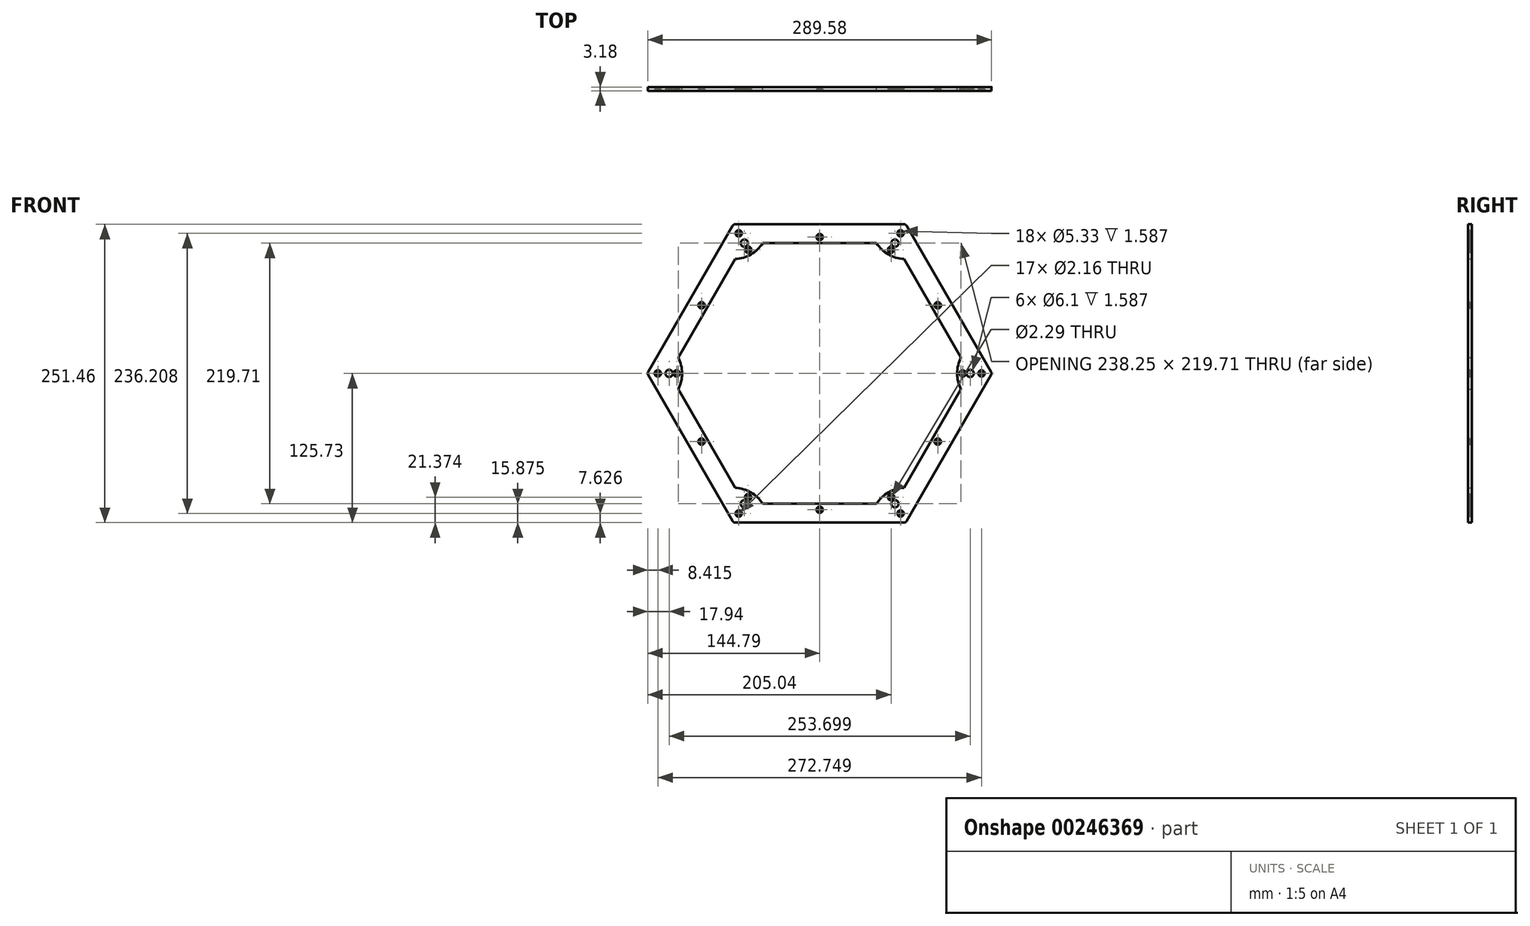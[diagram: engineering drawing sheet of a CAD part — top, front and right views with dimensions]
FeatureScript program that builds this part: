
annotation { "Feature Type Name" : "Feature", "Feature Type Description" : "" }
export const myFeature = defineFeature(function(context is Context, id is Id, definition is map)
    precondition{}
    {
        {
            var Q0;
            Q0=qCreatedBy(makeId("Front.planeOp"),FACE);
            var sketch = newSketch(context, id + "F0", { "sketchPlane" : qUnion([Q0])});
            skCircle(sketch, "E0.cCircle", {"center": v(0, 0) * mm, "radius": 125.73 * mm, "construction": true});
            skLineSegment(sketch, "E0.0", {"start": v(-72.6, 125.73) * mm, "end": v(72.6, 125.73) * mm});
            skLineSegment(sketch, "E0.1", {"start": v(72.6, 125.73) * mm, "end": v(145.18, 0) * mm});
            skLineSegment(sketch, "E0.2", {"start": v(145.18, 0) * mm, "end": v(72.6, -125.73) * mm});
            skLineSegment(sketch, "E0.3", {"start": v(72.6, -125.73) * mm, "end": v(-72.6, -125.73) * mm});
            skLineSegment(sketch, "E0.4", {"start": v(-72.6, -125.73) * mm, "end": v(-145.18, 0) * mm});
            skLineSegment(sketch, "E0.5", {"start": v(-145.18, 0) * mm, "end": v(-72.6, 125.73) * mm});
            skPoint(sketch, "E0.0.midPoint", {"position": v(0, 125.73) * mm});
            skLineSegment(sketch, "E1", {"start": v(0, 0) * mm, "end": v(-103.66, 179.55) * mm, "construction": true});
            skLineSegment(sketch, "E2", {"start": v(0, 0) * mm, "end": v(108.03, 187.1) * mm, "construction": true});
            skLineSegment(sketch, "E3", {"start": v(0, 0) * mm, "end": v(215.11, 0) * mm, "construction": true});
            skLineSegment(sketch, "E4", {"start": v(0, 0) * mm, "end": v(129.36, -224.05) * mm, "construction": true});
            skLineSegment(sketch, "E5", {"start": v(0, 0) * mm, "end": v(-137.05, -237.38) * mm, "construction": true});
            skLineSegment(sketch, "E6", {"start": v(0, 0) * mm, "end": v(-290.92, 0) * mm, "construction": true});
            skCircle(sketch, "E7.cCircle", {"center": v(0, 0) * mm, "radius": 109.86 * mm, "construction": true});
            skLineSegment(sketch, "E7.0", {"start": v(-63.42, 109.86) * mm, "end": v(63.42, 109.86) * mm});
            skLineSegment(sketch, "E7.1", {"start": v(63.42, 109.85) * mm, "end": v(126.85, 0) * mm});
            skLineSegment(sketch, "E7.2", {"start": v(126.85, 0) * mm, "end": v(63.42, -109.86) * mm});
            skLineSegment(sketch, "E7.3", {"start": v(63.42, -109.85) * mm, "end": v(-63.42, -109.86) * mm});
            skLineSegment(sketch, "E7.4", {"start": v(-63.42, -109.86) * mm, "end": v(-126.85, 0) * mm});
            skLineSegment(sketch, "E7.5", {"start": v(-126.85, 0) * mm, "end": v(-63.42, 109.86) * mm});
            skPoint(sketch, "E7.0.midPoint", {"position": v(0, 109.86) * mm});
            skCircle(sketch, "E8", {"center": v(-72.6, 125.73) * mm, "radius": 29.3 * mm});
            skCircle(sketch, "E9", {"center": v(72.6, 125.73) * mm, "radius": 29.3 * mm});
            skCircle(sketch, "E10", {"center": v(145.18, 0) * mm, "radius": 29.3 * mm});
            skCircle(sketch, "E11", {"center": v(72.6, -125.73) * mm, "radius": 29.3 * mm});
            skCircle(sketch, "E12", {"center": v(-72.6, -125.73) * mm, "radius": 29.3 * mm});
            skCircle(sketch, "E13", {"center": v(-145.18, 0) * mm, "radius": 29.3 * mm});
            skCircle(sketch, "E14", {"center": v(0, 0) * mm, "radius": 115.89 * mm, "construction": true});
            skSolve(sketch);
        }
        {
            var Q0;
            {var subQ0=sQuery(id+"F0.wireOp",EDGE,"E8");var subQ1=sQuery(id+"F0.wireOp",EDGE,"E0.0");var subQ2=makeQuery(id+"F0.imprint","INTERSECT",VERTEX,{"derivedFrom":[subQ1,subQ0]});Q0=makeQuery(id+"F0.imprint","IMPRINT",FACE,{"disambiguationData":[TD([[makeQuery(id+"F0.imprint","IMPRINT",EDGE,{"disambiguationData":[TD([[subQ2,-1.0]])],"derivedFrom":subQ1}),-1.0]])]});}
            var Q1;
            {var subQ6=sQuery(id+"F0.wireOp",EDGE,"E0.0");var subQ8=sQuery(id+"F0.wireOp",EDGE,"E0.5");var subQ9=makeQuery(id+"F0.imprint","INTERSECT",VERTEX,{"derivedFrom":[subQ6,subQ8]});Q1=makeQuery(id+"F0.imprint","IMPRINT",FACE,{"disambiguationData":[TD([[makeQuery(id+"F0.imprint","IMPRINT",EDGE,{"disambiguationData":[TD([[subQ9,-1.0]])],"derivedFrom":subQ6}),-1.0]])]});}
            var Q2;
            {var subQ0=sQuery(id+"F0.wireOp",EDGE,"E13");var subQ1=sQuery(id+"F0.wireOp",EDGE,"E0.5");var subQ2=makeQuery(id+"F0.imprint","INTERSECT",VERTEX,{"derivedFrom":[subQ1,subQ0]});Q2=makeQuery(id+"F0.imprint","IMPRINT",FACE,{"disambiguationData":[TD([[makeQuery(id+"F0.imprint","IMPRINT",EDGE,{"disambiguationData":[TD([[subQ2,-1.0]])],"derivedFrom":subQ1}),-1.0]])]});}
            var Q3;
            {var subQ6=sQuery(id+"F0.wireOp",EDGE,"E0.5");var subQ7=sQuery(id+"F0.wireOp",EDGE,"E0.4");var subQ8=makeQuery(id+"F0.imprint","INTERSECT",VERTEX,{"derivedFrom":[subQ7,subQ6]});Q3=makeQuery(id+"F0.imprint","IMPRINT",FACE,{"disambiguationData":[TD([[makeQuery(id+"F0.imprint","IMPRINT",EDGE,{"disambiguationData":[TD([[subQ8,1.0]])],"derivedFrom":subQ7}),-1.0]])]});}
            var Q4;
            {var subQ0=sQuery(id+"F0.wireOp",EDGE,"E7.5");var subQ1=sQuery(id+"F0.wireOp",EDGE,"E7.4");var subQ2=makeQuery(id+"F0.imprint","INTERSECT",VERTEX,{"derivedFrom":[subQ1,subQ0]});Q4=makeQuery(id+"F0.imprint","IMPRINT",FACE,{"disambiguationData":[TD([[makeQuery(id+"F0.imprint","IMPRINT",EDGE,{"disambiguationData":[TD([[subQ2,1.0]])],"derivedFrom":subQ1}),-1.0]])]});}
            var Q5;
            {var subQ0=sQuery(id+"F0.wireOp",EDGE,"E7.5");var subQ1=sQuery(id+"F0.wireOp",EDGE,"E7.0");var subQ2=makeQuery(id+"F0.imprint","INTERSECT",VERTEX,{"derivedFrom":[subQ1,subQ0]});Q5=makeQuery(id+"F0.imprint","IMPRINT",FACE,{"disambiguationData":[TD([[makeQuery(id+"F0.imprint","IMPRINT",EDGE,{"disambiguationData":[TD([[subQ2,-1.0]])],"derivedFrom":subQ1}),-1.0]])]});}
            var Q6;
            {var subQ0=sQuery(id+"F0.wireOp",EDGE,"E7.1");var subQ1=sQuery(id+"F0.wireOp",EDGE,"E7.0");var subQ2=makeQuery(id+"F0.imprint","INTERSECT",VERTEX,{"derivedFrom":[subQ1,subQ0]});Q6=makeQuery(id+"F0.imprint","IMPRINT",FACE,{"disambiguationData":[TD([[makeQuery(id+"F0.imprint","IMPRINT",EDGE,{"disambiguationData":[TD([[subQ2,1.0]])],"derivedFrom":subQ1}),-1.0]])]});}
            var Q7;
            {var subQ6=sQuery(id+"F0.wireOp",EDGE,"E0.1");var subQ7=sQuery(id+"F0.wireOp",EDGE,"E0.0");var subQ8=makeQuery(id+"F0.imprint","INTERSECT",VERTEX,{"derivedFrom":[subQ7,subQ6]});Q7=makeQuery(id+"F0.imprint","IMPRINT",FACE,{"disambiguationData":[TD([[makeQuery(id+"F0.imprint","IMPRINT",EDGE,{"disambiguationData":[TD([[subQ8,1.0]])],"derivedFrom":subQ7}),-1.0]])]});}
            var Q8;
            {var subQ0=sQuery(id+"F0.wireOp",EDGE,"E9");var subQ1=sQuery(id+"F0.wireOp",EDGE,"E0.1");var subQ2=makeQuery(id+"F0.imprint","INTERSECT",VERTEX,{"derivedFrom":[subQ1,subQ0]});Q8=makeQuery(id+"F0.imprint","IMPRINT",FACE,{"disambiguationData":[TD([[makeQuery(id+"F0.imprint","IMPRINT",EDGE,{"disambiguationData":[TD([[subQ2,-1.0]])],"derivedFrom":subQ1}),-1.0]])]});}
            var Q9;
            {var subQ0=sQuery(id+"F0.wireOp",EDGE,"E7.2");var subQ1=sQuery(id+"F0.wireOp",EDGE,"E7.1");var subQ2=makeQuery(id+"F0.imprint","INTERSECT",VERTEX,{"derivedFrom":[subQ1,subQ0]});Q9=makeQuery(id+"F0.imprint","IMPRINT",FACE,{"disambiguationData":[TD([[makeQuery(id+"F0.imprint","IMPRINT",EDGE,{"disambiguationData":[TD([[subQ2,1.0]])],"derivedFrom":subQ1}),-1.0]])]});}
            var Q10;
            {var subQ5=sQuery(id+"F0.wireOp",EDGE,"E0.2");var subQ6=sQuery(id+"F0.wireOp",EDGE,"E0.1");var subQ7=makeQuery(id+"F0.imprint","INTERSECT",VERTEX,{"derivedFrom":[subQ6,subQ5]});Q10=makeQuery(id+"F0.imprint","IMPRINT",FACE,{"disambiguationData":[TD([[makeQuery(id+"F0.imprint","IMPRINT",EDGE,{"disambiguationData":[TD([[subQ7,1.0]])],"derivedFrom":subQ6}),-1.0]])]});}
            var Q11;
            {var subQ0=sQuery(id+"F0.wireOp",EDGE,"E10");var subQ1=sQuery(id+"F0.wireOp",EDGE,"E0.2");var subQ2=makeQuery(id+"F0.imprint","INTERSECT",VERTEX,{"derivedFrom":[subQ1,subQ0]});Q11=makeQuery(id+"F0.imprint","IMPRINT",FACE,{"disambiguationData":[TD([[makeQuery(id+"F0.imprint","IMPRINT",EDGE,{"disambiguationData":[TD([[subQ2,-1.0]])],"derivedFrom":subQ1}),-1.0]])]});}
            var Q12;
            {var subQ6=sQuery(id+"F0.wireOp",EDGE,"E0.3");var subQ7=sQuery(id+"F0.wireOp",EDGE,"E0.2");var subQ8=makeQuery(id+"F0.imprint","INTERSECT",VERTEX,{"derivedFrom":[subQ7,subQ6]});Q12=makeQuery(id+"F0.imprint","IMPRINT",FACE,{"disambiguationData":[TD([[makeQuery(id+"F0.imprint","IMPRINT",EDGE,{"disambiguationData":[TD([[subQ8,1.0]])],"derivedFrom":subQ7}),-1.0]])]});}
            var Q13;
            {var subQ0=sQuery(id+"F0.wireOp",EDGE,"E7.3");var subQ1=sQuery(id+"F0.wireOp",EDGE,"E7.2");var subQ2=makeQuery(id+"F0.imprint","INTERSECT",VERTEX,{"derivedFrom":[subQ1,subQ0]});Q13=makeQuery(id+"F0.imprint","IMPRINT",FACE,{"disambiguationData":[TD([[makeQuery(id+"F0.imprint","IMPRINT",EDGE,{"disambiguationData":[TD([[subQ2,1.0]])],"derivedFrom":subQ1}),-1.0]])]});}
            var Q14;
            {var subQ0=sQuery(id+"F0.wireOp",EDGE,"E11");var subQ1=sQuery(id+"F0.wireOp",EDGE,"E0.3");var subQ2=makeQuery(id+"F0.imprint","INTERSECT",VERTEX,{"derivedFrom":[subQ1,subQ0]});Q14=makeQuery(id+"F0.imprint","IMPRINT",FACE,{"disambiguationData":[TD([[makeQuery(id+"F0.imprint","IMPRINT",EDGE,{"disambiguationData":[TD([[subQ2,-1.0]])],"derivedFrom":subQ1}),-1.0]])]});}
            var Q15;
            {var subQ6=sQuery(id+"F0.wireOp",EDGE,"E0.4");var subQ8=sQuery(id+"F0.wireOp",EDGE,"E0.3");var subQ9=makeQuery(id+"F0.imprint","INTERSECT",VERTEX,{"derivedFrom":[subQ8,subQ6]});Q15=makeQuery(id+"F0.imprint","IMPRINT",FACE,{"disambiguationData":[TD([[makeQuery(id+"F0.imprint","IMPRINT",EDGE,{"disambiguationData":[TD([[subQ9,1.0]])],"derivedFrom":subQ8}),-1.0]])]});}
            var Q16;
            {var subQ0=sQuery(id+"F0.wireOp",EDGE,"E7.4");var subQ1=sQuery(id+"F0.wireOp",EDGE,"E7.3");var subQ2=makeQuery(id+"F0.imprint","INTERSECT",VERTEX,{"derivedFrom":[subQ1,subQ0]});Q16=makeQuery(id+"F0.imprint","IMPRINT",FACE,{"disambiguationData":[TD([[makeQuery(id+"F0.imprint","IMPRINT",EDGE,{"disambiguationData":[TD([[subQ2,1.0]])],"derivedFrom":subQ1}),-1.0]])]});}
            var Q17;
            {var subQ0=sQuery(id+"F0.wireOp",EDGE,"E12");var subQ1=sQuery(id+"F0.wireOp",EDGE,"E0.4");var subQ2=makeQuery(id+"F0.imprint","INTERSECT",VERTEX,{"derivedFrom":[subQ1,subQ0]});Q17=makeQuery(id+"F0.imprint","IMPRINT",FACE,{"disambiguationData":[TD([[makeQuery(id+"F0.imprint","IMPRINT",EDGE,{"disambiguationData":[TD([[subQ2,-1.0]])],"derivedFrom":subQ1}),-1.0]])]});}
            extrude(context, id + "F1", {"entities" : qUnion([Q0, Q1, Q2, Q3, Q4, Q5, Q6, Q7, Q8, Q9, Q10, Q11, Q12, Q13, Q14, Q15, Q16, Q17]), "depth" : 3.17 * mm});
        }
        {
            var Q0;
            Q0=makeQuery(id+"F1.opExtrude","CAP_FACE",FACE,{"disambiguationData":[OSD([sQuery(id+"F0.wireOp",EDGE,"E0.0"),sQuery(id+"F0.wireOp",EDGE,"E0.1"),sQuery(id+"F0.wireOp",EDGE,"E0.2"),sQuery(id+"F0.wireOp",EDGE,"E0.3"),sQuery(id+"F0.wireOp",EDGE,"E0.4"),sQuery(id+"F0.wireOp",EDGE,"E0.5"),sQuery(id+"F0.wireOp",EDGE,"E7.0"),sQuery(id+"F0.wireOp",EDGE,"E7.1"),sQuery(id+"F0.wireOp",EDGE,"E7.2"),sQuery(id+"F0.wireOp",EDGE,"E7.3"),sQuery(id+"F0.wireOp",EDGE,"E7.4"),sQuery(id+"F0.wireOp",EDGE,"E7.5"),sQuery(id+"F0.wireOp",EDGE,"E8"),sQuery(id+"F0.wireOp",EDGE,"E9"),sQuery(id+"F0.wireOp",EDGE,"E10"),sQuery(id+"F0.wireOp",EDGE,"E11"),sQuery(id+"F0.wireOp",EDGE,"E12"),sQuery(id+"F0.wireOp",EDGE,"E13")])],"isStart":false});
            var sketch = newSketch(context, id + "F2", { "sketchPlane" : qUnion([Q0])});
            skCircle(sketch, "E15", {"center": v(-63.42, 109.86) * mm, "radius": 3.05 * mm});
            skCircle(sketch, "E16", {"center": v(63.42, 109.86) * mm, "radius": 3.05 * mm});
            skCircle(sketch, "E17", {"center": v(-126.85, 0) * mm, "radius": 3.05 * mm});
            skCircle(sketch, "E18", {"center": v(-63.42, -109.86) * mm, "radius": 3.05 * mm});
            skCircle(sketch, "E19", {"center": v(63.42, -109.85) * mm, "radius": 3.05 * mm});
            skCircle(sketch, "E20", {"center": v(126.85, 0) * mm, "radius": 3.05 * mm});
            skSolve(sketch);
        }
        {
            var Q0;
            Q0 = qSketchRegion(id + "F2", true);
            extrude(context, id + "F3", {"entities" : qUnion([Q0]), "operationType" : NewBodyOperationType.REMOVE, "oppositeDirection" : true, "depth" : 1.59 * mm});
        }
        {
            var Q0;
            Q0=makeQuery(id+"F1.opExtrude","CAP_FACE",FACE,{"disambiguationData":[OSD([sQuery(id+"F0.wireOp",EDGE,"E0.0"),sQuery(id+"F0.wireOp",EDGE,"E0.1"),sQuery(id+"F0.wireOp",EDGE,"E0.2"),sQuery(id+"F0.wireOp",EDGE,"E0.3"),sQuery(id+"F0.wireOp",EDGE,"E0.4"),sQuery(id+"F0.wireOp",EDGE,"E0.5"),sQuery(id+"F0.wireOp",EDGE,"E7.0"),sQuery(id+"F0.wireOp",EDGE,"E7.1"),sQuery(id+"F0.wireOp",EDGE,"E7.2"),sQuery(id+"F0.wireOp",EDGE,"E7.3"),sQuery(id+"F0.wireOp",EDGE,"E7.4"),sQuery(id+"F0.wireOp",EDGE,"E7.5"),sQuery(id+"F0.wireOp",EDGE,"E8"),sQuery(id+"F0.wireOp",EDGE,"E9"),sQuery(id+"F0.wireOp",EDGE,"E10"),sQuery(id+"F0.wireOp",EDGE,"E11"),sQuery(id+"F0.wireOp",EDGE,"E12"),sQuery(id+"F0.wireOp",EDGE,"E13")])],"isStart":false});
            var sketch = newSketch(context, id + "F4", { "sketchPlane" : qUnion([Q0])});
            skCircle(sketch, "E21", {"center": v(-60.25, 104.36) * mm, "radius": 1.08 * mm});
            skLineSegment(sketch, "E22", {"start": v(-63.42, 109.86) * mm, "end": v(-60.25, 104.36) * mm, "construction": true});
            skLineSegment(sketch, "E23", {"start": v(63.42, 109.86) * mm, "end": v(60.25, 104.36) * mm, "construction": true});
            skLineSegment(sketch, "E24", {"start": v(126.85, 0) * mm, "end": v(120.5, 0) * mm, "construction": true});
            skLineSegment(sketch, "E25", {"start": v(63.42, -109.86) * mm, "end": v(60.25, -104.36) * mm, "construction": true});
            skLineSegment(sketch, "E26", {"start": v(-63.42, -109.86) * mm, "end": v(-60.25, -104.36) * mm, "construction": true});
            skLineSegment(sketch, "E27", {"start": v(-126.85, 0) * mm, "end": v(-120.5, 0) * mm, "construction": true});
            skCircle(sketch, "E28", {"center": v(60.25, 104.36) * mm, "radius": 1.08 * mm});
            skCircle(sketch, "E29", {"center": v(120.5, 0) * mm, "radius": 1.08 * mm});
            skCircle(sketch, "E30", {"center": v(60.25, -104.36) * mm, "radius": 1.14 * mm});
            skCircle(sketch, "E31", {"center": v(-60.25, -104.36) * mm, "radius": 1.08 * mm});
            skCircle(sketch, "E32", {"center": v(-120.5, 0) * mm, "radius": 1.08 * mm});
            skCircle(sketch, "E33", {"center": v(-120.5, 0) * mm, "radius": 2.67 * mm});
            skCircle(sketch, "E34", {"center": v(-60.25, 104.36) * mm, "radius": 2.67 * mm});
            skCircle(sketch, "E35", {"center": v(60.25, 104.36) * mm, "radius": 2.67 * mm});
            skCircle(sketch, "E36", {"center": v(120.5, 0) * mm, "radius": 2.67 * mm});
            skCircle(sketch, "E37", {"center": v(60.25, -104.36) * mm, "radius": 2.67 * mm});
            skCircle(sketch, "E38", {"center": v(-60.25, -104.36) * mm, "radius": 2.67 * mm});
            skCircle(sketch, "E39", {"center": v(-68.19, 118.1) * mm, "radius": 2.67 * mm});
            skLineSegment(sketch, "E40", {"start": v(-63.42, 109.86) * mm, "end": v(-68.19, 118.1) * mm, "construction": true});
            skCircle(sketch, "E41", {"center": v(-68.19, 118.1) * mm, "radius": 1.08 * mm});
            skLineSegment(sketch, "E42", {"start": v(63.42, 109.86) * mm, "end": v(68.19, 118.1) * mm, "construction": true});
            skCircle(sketch, "E43", {"center": v(68.19, 118.1) * mm, "radius": 2.67 * mm});
            skCircle(sketch, "E44", {"center": v(68.19, 118.1) * mm, "radius": 1.08 * mm});
            skLineSegment(sketch, "E45", {"start": v(-126.85, 0) * mm, "end": v(-136.37, 0) * mm, "construction": true});
            skCircle(sketch, "E46", {"center": v(-136.37, 0) * mm, "radius": 2.67 * mm});
            skCircle(sketch, "E47", {"center": v(-136.37, 0) * mm, "radius": 1.08 * mm});
            skLineSegment(sketch, "E48", {"start": v(-63.42, -109.86) * mm, "end": v(-68.19, -118.1) * mm, "construction": true});
            skCircle(sketch, "E49", {"center": v(-68.19, -118.1) * mm, "radius": 2.67 * mm});
            skCircle(sketch, "E50", {"center": v(-68.19, -118.1) * mm, "radius": 1.08 * mm});
            skLineSegment(sketch, "E51", {"start": v(126.85, 0) * mm, "end": v(136.37, 0) * mm, "construction": true});
            skCircle(sketch, "E52", {"center": v(136.37, 0) * mm, "radius": 2.67 * mm});
            skCircle(sketch, "E53", {"center": v(136.37, 0) * mm, "radius": 1.08 * mm});
            skLineSegment(sketch, "E54", {"start": v(63.42, -109.86) * mm, "end": v(68.19, -118.1) * mm, "construction": true});
            skCircle(sketch, "E55", {"center": v(68.19, -118.1) * mm, "radius": 2.67 * mm});
            skCircle(sketch, "E56", {"center": v(68.19, -118.1) * mm, "radius": 1.08 * mm});
            skCircle(sketch, "E57", {"center": v(0, 114.94) * mm, "radius": 2.67 * mm});
            skCircle(sketch, "E58", {"center": v(0, 114.94) * mm, "radius": 1.08 * mm});
            skCircle(sketch, "E59.1.0", {"center": v(-99.54, 57.47) * mm, "radius": 1.08 * mm});
            skCircle(sketch, "E59.1.1", {"center": v(-99.54, 57.47) * mm, "radius": 2.67 * mm});
            skCircle(sketch, "E59.2.0", {"center": v(-99.54, -57.47) * mm, "radius": 1.08 * mm});
            skCircle(sketch, "E59.2.1", {"center": v(-99.54, -57.47) * mm, "radius": 2.67 * mm});
            skCircle(sketch, "E59.3.0", {"center": v(0, -114.94) * mm, "radius": 1.08 * mm});
            skCircle(sketch, "E59.3.1", {"center": v(0, -114.94) * mm, "radius": 2.67 * mm});
            skCircle(sketch, "E59.4.0", {"center": v(99.54, -57.47) * mm, "radius": 1.08 * mm});
            skCircle(sketch, "E59.4.1", {"center": v(99.54, -57.47) * mm, "radius": 2.67 * mm});
            skCircle(sketch, "E59.5.0", {"center": v(99.54, 57.47) * mm, "radius": 1.08 * mm});
            skCircle(sketch, "E59.5.1", {"center": v(99.54, 57.47) * mm, "radius": 2.67 * mm});
            skPoint(sketch, "E59.center", {"position": v(0, 0) * mm});
            skLineSegment(sketch, "E60", {"start": v(0, 0) * mm, "end": v(99.54, 57.47) * mm, "construction": true});
            skLineSegment(sketch, "E61", {"start": v(0, 0) * mm, "end": v(0, -114.94) * mm, "construction": true});
            skLineSegment(sketch, "E62", {"start": v(0, 0) * mm, "end": v(99.54, -57.47) * mm, "construction": true});
            skLineSegment(sketch, "E63", {"start": v(0, 0) * mm, "end": v(-99.54, -57.47) * mm, "construction": true});
            skLineSegment(sketch, "E64", {"start": v(0, 0) * mm, "end": v(0, 114.94) * mm, "construction": true});
            skLineSegment(sketch, "E65", {"start": v(0, 0) * mm, "end": v(-99.54, 57.47) * mm, "construction": true});
            skSolve(sketch);
        }
        {
            var Q0;
            Q0=makeQuery(id+"F4.imprint","IMPRINT",FACE,{"disambiguationData":[TD([[makeQuery(id+"F4.imprint","IMPRINT",EDGE,{"derivedFrom":sQuery(id+"F4.wireOp",EDGE,"E32")}),-1.0]])]});
            var Q1;
            Q1=makeQuery(id+"F4.imprint","IMPRINT",FACE,{"disambiguationData":[TD([[makeQuery(id+"F4.imprint","IMPRINT",EDGE,{"derivedFrom":sQuery(id+"F4.wireOp",EDGE,"E21")}),-1.0]])]});
            var Q2;
            Q2=makeQuery(id+"F4.imprint","IMPRINT",FACE,{"disambiguationData":[TD([[makeQuery(id+"F4.imprint","IMPRINT",EDGE,{"derivedFrom":sQuery(id+"F4.wireOp",EDGE,"E28")}),-1.0]])]});
            var Q3;
            Q3=makeQuery(id+"F4.imprint","IMPRINT",FACE,{"disambiguationData":[TD([[makeQuery(id+"F4.imprint","IMPRINT",EDGE,{"derivedFrom":sQuery(id+"F4.wireOp",EDGE,"E29")}),-1.0]])]});
            var Q4;
            Q4=makeQuery(id+"F4.imprint","IMPRINT",FACE,{"disambiguationData":[TD([[makeQuery(id+"F4.imprint","IMPRINT",EDGE,{"derivedFrom":sQuery(id+"F4.wireOp",EDGE,"E30")}),-1.0]])]});
            var Q5;
            Q5=makeQuery(id+"F4.imprint","IMPRINT",FACE,{"disambiguationData":[TD([[makeQuery(id+"F4.imprint","IMPRINT",EDGE,{"derivedFrom":sQuery(id+"F4.wireOp",EDGE,"E31")}),-1.0]])]});
            var Q6;
            Q6=makeQuery(id+"F4.imprint","IMPRINT",FACE,{"disambiguationData":[TD([[makeQuery(id+"F4.imprint","IMPRINT",EDGE,{"derivedFrom":sQuery(id+"F4.wireOp",EDGE,"E49")}),1.0]])]});
            var Q7;
            Q7=makeQuery(id+"F4.imprint","IMPRINT",FACE,{"disambiguationData":[TD([[makeQuery(id+"F4.imprint","IMPRINT",EDGE,{"derivedFrom":sQuery(id+"F4.wireOp",EDGE,"E55")}),1.0]])]});
            var Q8;
            Q8=makeQuery(id+"F4.imprint","IMPRINT",FACE,{"disambiguationData":[TD([[makeQuery(id+"F4.imprint","IMPRINT",EDGE,{"derivedFrom":sQuery(id+"F4.wireOp",EDGE,"E52")}),1.0]])]});
            var Q9;
            Q9=makeQuery(id+"F4.imprint","IMPRINT",FACE,{"disambiguationData":[TD([[makeQuery(id+"F4.imprint","IMPRINT",EDGE,{"derivedFrom":sQuery(id+"F4.wireOp",EDGE,"E43")}),1.0]])]});
            var Q10;
            Q10=makeQuery(id+"F4.imprint","IMPRINT",FACE,{"disambiguationData":[TD([[makeQuery(id+"F4.imprint","IMPRINT",EDGE,{"derivedFrom":sQuery(id+"F4.wireOp",EDGE,"E39")}),1.0]])]});
            var Q11;
            Q11=makeQuery(id+"F4.imprint","IMPRINT",FACE,{"disambiguationData":[TD([[makeQuery(id+"F4.imprint","IMPRINT",EDGE,{"derivedFrom":sQuery(id+"F4.wireOp",EDGE,"E46")}),1.0]])]});
            var Q12;
            Q12=makeQuery(id+"F4.imprint","IMPRINT",FACE,{"disambiguationData":[TD([[makeQuery(id+"F4.imprint","IMPRINT",EDGE,{"derivedFrom":sQuery(id+"F4.wireOp",EDGE,"E59.1.0")}),-1.0]])]});
            var Q13;
            Q13=makeQuery(id+"F4.imprint","IMPRINT",FACE,{"disambiguationData":[TD([[makeQuery(id+"F4.imprint","IMPRINT",EDGE,{"derivedFrom":sQuery(id+"F4.wireOp",EDGE,"E57")}),1.0]])]});
            var Q14;
            Q14=makeQuery(id+"F4.imprint","IMPRINT",FACE,{"disambiguationData":[TD([[makeQuery(id+"F4.imprint","IMPRINT",EDGE,{"derivedFrom":sQuery(id+"F4.wireOp",EDGE,"E59.5.0")}),-1.0]])]});
            var Q15;
            Q15=makeQuery(id+"F4.imprint","IMPRINT",FACE,{"disambiguationData":[TD([[makeQuery(id+"F4.imprint","IMPRINT",EDGE,{"derivedFrom":sQuery(id+"F4.wireOp",EDGE,"E59.4.0")}),-1.0]])]});
            var Q16;
            Q16=makeQuery(id+"F4.imprint","IMPRINT",FACE,{"disambiguationData":[TD([[makeQuery(id+"F4.imprint","IMPRINT",EDGE,{"derivedFrom":sQuery(id+"F4.wireOp",EDGE,"E59.3.0")}),-1.0]])]});
            var Q17;
            Q17=makeQuery(id+"F4.imprint","IMPRINT",FACE,{"disambiguationData":[TD([[makeQuery(id+"F4.imprint","IMPRINT",EDGE,{"derivedFrom":sQuery(id+"F4.wireOp",EDGE,"E59.2.0")}),-1.0]])]});
            extrude(context, id + "F5", {"entities" : qUnion([Q0, Q1, Q2, Q3, Q4, Q5, Q6, Q7, Q8, Q9, Q10, Q11, Q12, Q13, Q14, Q15, Q16, Q17]), "operationType" : NewBodyOperationType.REMOVE, "oppositeDirection" : true, "depth" : 1.59 * mm});
        }
        {
            var Q0;
            Q0=makeQuery(id+"F4.imprint","IMPRINT",FACE,{"disambiguationData":[TD([[makeQuery(id+"F4.imprint","IMPRINT",EDGE,{"derivedFrom":sQuery(id+"F4.wireOp",EDGE,"E31")}),1.0]])]});
            var Q1;
            Q1=makeQuery(id+"F4.imprint","IMPRINT",FACE,{"disambiguationData":[TD([[makeQuery(id+"F4.imprint","IMPRINT",EDGE,{"derivedFrom":sQuery(id+"F4.wireOp",EDGE,"E32")}),1.0]])]});
            var Q2;
            Q2=makeQuery(id+"F4.imprint","IMPRINT",FACE,{"disambiguationData":[TD([[makeQuery(id+"F4.imprint","IMPRINT",EDGE,{"derivedFrom":sQuery(id+"F4.wireOp",EDGE,"E21")}),1.0]])]});
            var Q3;
            Q3=makeQuery(id+"F4.imprint","IMPRINT",FACE,{"disambiguationData":[TD([[makeQuery(id+"F4.imprint","IMPRINT",EDGE,{"derivedFrom":sQuery(id+"F4.wireOp",EDGE,"E28")}),1.0]])]});
            var Q4;
            Q4=makeQuery(id+"F4.imprint","IMPRINT",FACE,{"disambiguationData":[TD([[makeQuery(id+"F4.imprint","IMPRINT",EDGE,{"derivedFrom":sQuery(id+"F4.wireOp",EDGE,"E29")}),1.0]])]});
            var Q5;
            Q5=makeQuery(id+"F4.imprint","IMPRINT",FACE,{"disambiguationData":[TD([[makeQuery(id+"F4.imprint","IMPRINT",EDGE,{"derivedFrom":sQuery(id+"F4.wireOp",EDGE,"E30")}),1.0]])]});
            var Q6;
            Q6=makeQuery(id+"F4.imprint","IMPRINT",FACE,{"disambiguationData":[TD([[makeQuery(id+"F4.imprint","IMPRINT",EDGE,{"derivedFrom":sQuery(id+"F4.wireOp",EDGE,"E47")}),1.0]])]});
            var Q7;
            Q7=makeQuery(id+"F4.imprint","IMPRINT",FACE,{"disambiguationData":[TD([[makeQuery(id+"F4.imprint","IMPRINT",EDGE,{"derivedFrom":sQuery(id+"F4.wireOp",EDGE,"E50")}),1.0]])]});
            var Q8;
            Q8=makeQuery(id+"F4.imprint","IMPRINT",FACE,{"disambiguationData":[TD([[makeQuery(id+"F4.imprint","IMPRINT",EDGE,{"derivedFrom":sQuery(id+"F4.wireOp",EDGE,"E56")}),1.0]])]});
            var Q9;
            Q9=makeQuery(id+"F4.imprint","IMPRINT",FACE,{"disambiguationData":[TD([[makeQuery(id+"F4.imprint","IMPRINT",EDGE,{"derivedFrom":sQuery(id+"F4.wireOp",EDGE,"E53")}),1.0]])]});
            var Q10;
            Q10=makeQuery(id+"F4.imprint","IMPRINT",FACE,{"disambiguationData":[TD([[makeQuery(id+"F4.imprint","IMPRINT",EDGE,{"derivedFrom":sQuery(id+"F4.wireOp",EDGE,"E44")}),1.0]])]});
            var Q11;
            Q11=makeQuery(id+"F4.imprint","IMPRINT",FACE,{"disambiguationData":[TD([[makeQuery(id+"F4.imprint","IMPRINT",EDGE,{"derivedFrom":sQuery(id+"F4.wireOp",EDGE,"E41")}),1.0]])]});
            var Q12;
            Q12=makeQuery(id+"F4.imprint","IMPRINT",FACE,{"disambiguationData":[TD([[makeQuery(id+"F4.imprint","IMPRINT",EDGE,{"derivedFrom":sQuery(id+"F4.wireOp",EDGE,"E59.1.0")}),1.0]])]});
            var Q13;
            Q13=makeQuery(id+"F4.imprint","IMPRINT",FACE,{"disambiguationData":[TD([[makeQuery(id+"F4.imprint","IMPRINT",EDGE,{"derivedFrom":sQuery(id+"F4.wireOp",EDGE,"E59.2.0")}),1.0]])]});
            var Q14;
            Q14=makeQuery(id+"F4.imprint","IMPRINT",FACE,{"disambiguationData":[TD([[makeQuery(id+"F4.imprint","IMPRINT",EDGE,{"derivedFrom":sQuery(id+"F4.wireOp",EDGE,"E59.3.0")}),1.0]])]});
            var Q15;
            Q15=makeQuery(id+"F4.imprint","IMPRINT",FACE,{"disambiguationData":[TD([[makeQuery(id+"F4.imprint","IMPRINT",EDGE,{"derivedFrom":sQuery(id+"F4.wireOp",EDGE,"E59.4.0")}),1.0]])]});
            var Q16;
            Q16=makeQuery(id+"F4.imprint","IMPRINT",FACE,{"disambiguationData":[TD([[makeQuery(id+"F4.imprint","IMPRINT",EDGE,{"derivedFrom":sQuery(id+"F4.wireOp",EDGE,"E59.5.0")}),1.0]])]});
            var Q17;
            Q17=makeQuery(id+"F4.imprint","IMPRINT",FACE,{"disambiguationData":[TD([[makeQuery(id+"F4.imprint","IMPRINT",EDGE,{"derivedFrom":sQuery(id+"F4.wireOp",EDGE,"E58")}),1.0]])]});
            extrude(context, id + "F6", {"entities" : qUnion([Q0, Q1, Q2, Q3, Q4, Q5, Q6, Q7, Q8, Q9, Q10, Q11, Q12, Q13, Q14, Q15, Q16, Q17]), "operationType" : NewBodyOperationType.REMOVE, "endBound" : BoundingType.THROUGH_ALL, "oppositeDirection" : true, "depth" : 25.4 * mm});
        }
        {
            var Q0;
            Q0=makeQuery(id+"F1.opExtrude","SWEPT_EDGE",EDGE,{"disambiguationData":[OSD([sQuery(id+"F0.wireOp",EDGE,"E0.0"),sQuery(id+"F0.wireOp",EDGE,"E0.5")])]});
            var Q1;
            Q1=makeQuery(id+"F1.opExtrude","SWEPT_EDGE",EDGE,{"disambiguationData":[OSD([sQuery(id+"F0.wireOp",EDGE,"E0.0"),sQuery(id+"F0.wireOp",EDGE,"E0.1")])]});
            var Q2;
            Q2=makeQuery(id+"F1.opExtrude","SWEPT_EDGE",EDGE,{"disambiguationData":[OSD([sQuery(id+"F0.wireOp",EDGE,"E0.1"),sQuery(id+"F0.wireOp",EDGE,"E0.2")])]});
            var Q3;
            Q3=makeQuery(id+"F1.opExtrude","SWEPT_EDGE",EDGE,{"disambiguationData":[OSD([sQuery(id+"F0.wireOp",EDGE,"E0.2"),sQuery(id+"F0.wireOp",EDGE,"E0.3")])]});
            var Q4;
            Q4=makeQuery(id+"F1.opExtrude","SWEPT_EDGE",EDGE,{"disambiguationData":[OSD([sQuery(id+"F0.wireOp",EDGE,"E0.3"),sQuery(id+"F0.wireOp",EDGE,"E0.4")])]});
            var Q5;
            Q5=makeQuery(id+"F1.opExtrude","SWEPT_EDGE",EDGE,{"disambiguationData":[OSD([sQuery(id+"F0.wireOp",EDGE,"E0.4"),sQuery(id+"F0.wireOp",EDGE,"E0.5")])]});
            fillet(context, id + "F7", {"entities" : qUnion([Q0, Q1, Q2, Q3, Q4, Q5]), "radius" : 2.54 * mm, "tangentPropagation" : true, "allowEdgeOverflow" : false});
        }
    });
